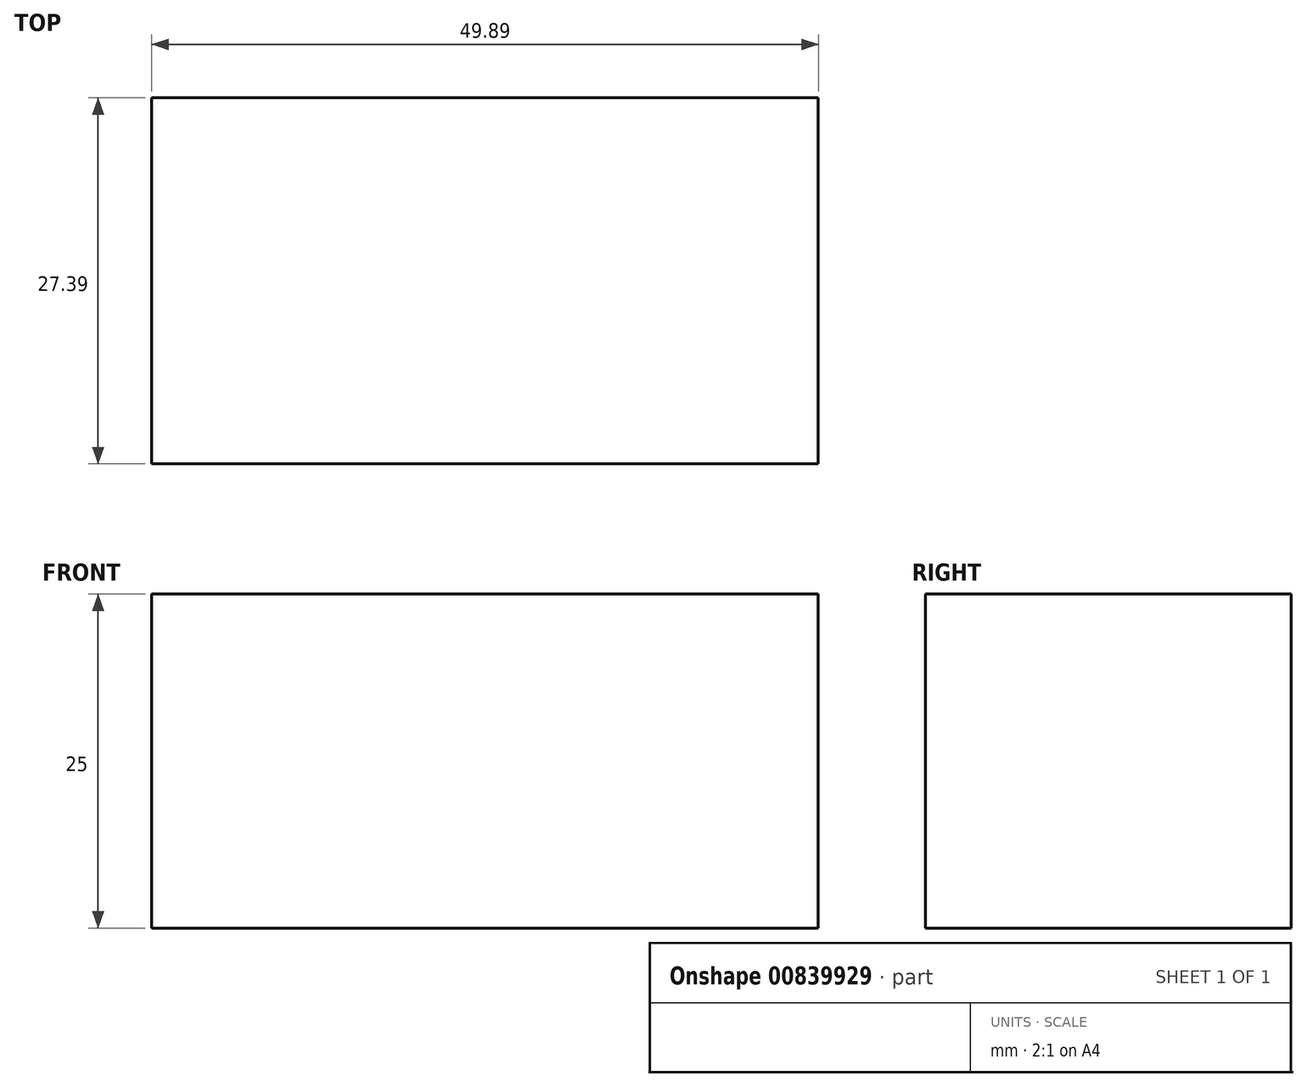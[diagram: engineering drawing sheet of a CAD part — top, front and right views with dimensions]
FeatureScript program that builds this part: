
annotation { "Feature Type Name" : "Feature", "Feature Type Description" : "" }
export const myFeature = defineFeature(function(context is Context, id is Id, definition is map)
    precondition{}
    {
        {
            var Q0;
            Q0=qCreatedBy(makeId("Top.planeOp"),FACE);
            var sketch = newSketch(context, id + "F0", { "sketchPlane" : qUnion([Q0])});
            skLineSegment(sketch, "E0.bottom", {"start": v(-21.68, 13.37) * mm, "end": v(28.2, 13.37) * mm});
            skLineSegment(sketch, "E0.top", {"start": v(-21.68, -14.02) * mm, "end": v(28.2, -14.02) * mm});
            skLineSegment(sketch, "E0.left", {"start": v(-21.68, 13.37) * mm, "end": v(-21.68, -14.02) * mm});
            skLineSegment(sketch, "E0.right", {"start": v(28.2, 13.37) * mm, "end": v(28.2, -14.02) * mm});
            skText(sketch, "E1", { "text": "Ashu", "fontName": "OpenSans-Regular.ttf"});
            const initialGuessF0  = {"E1": [0.00049, -0.00652, 1, 0, 0.00359]};
            skSetInitialGuess(sketch, initialGuessF0);
            skSolve(sketch);
        }
        {
            var Q0;
            Q0=makeQuery(id+"F0.imprint","IMPRINT",FACE,{"disambiguationData":[TD([[makeQuery(id+"F0.imprint","IMPRINT",EDGE,{"derivedFrom":sQuery(id+"F0.wireOp",EDGE,"E0.bottom")}),-1.0]])]});
            var Q1;
            Q1=makeQuery(id+"F0.imprint","IMPRINT",FACE,{"disambiguationData":[TD([[makeQuery(id+"F0.imprint","IMPRINT",EDGE,{"derivedFrom":sQuery(id+"F0.wireOp",EDGE,"E1.sketch_text.stroke-0")}),-1.0]])]});
            var Q2;
            Q2=makeQuery(id+"F0.imprint","IMPRINT",FACE,{"disambiguationData":[TD([[makeQuery(id+"F0.imprint","IMPRINT",EDGE,{"derivedFrom":sQuery(id+"F0.wireOp",EDGE,"E1.sketch_text.stroke-8")}),1.0]])]});
            var Q3;
            Q3=makeQuery(id+"F0.imprint","IMPRINT",FACE,{"disambiguationData":[TD([[makeQuery(id+"F0.imprint","IMPRINT",EDGE,{"derivedFrom":sQuery(id+"F0.wireOp",EDGE,"E1.sketch_text.stroke-38")}),-1.0]])]});
            var Q4;
            Q4=makeQuery(id+"F0.imprint","IMPRINT",FACE,{"disambiguationData":[TD([[makeQuery(id+"F0.imprint","IMPRINT",EDGE,{"derivedFrom":sQuery(id+"F0.wireOp",EDGE,"E1.sketch_text.stroke-56")}),-1.0]])]});
            var Q5;
            Q5=makeQuery(id+"F0.imprint","IMPRINT",FACE,{"disambiguationData":[TD([[makeQuery(id+"F0.imprint","IMPRINT",EDGE,{"derivedFrom":sQuery(id+"F0.wireOp",EDGE,"E1.sketch_text.stroke-13")}),-1.0]])]});
            extrude(context, id + "F1", {"entities" : qUnion([Q0, Q1, Q2, Q3, Q4, Q5]), "depth" : 25 * mm, "offsetDistance" : 25 * mm});
        }
    });
